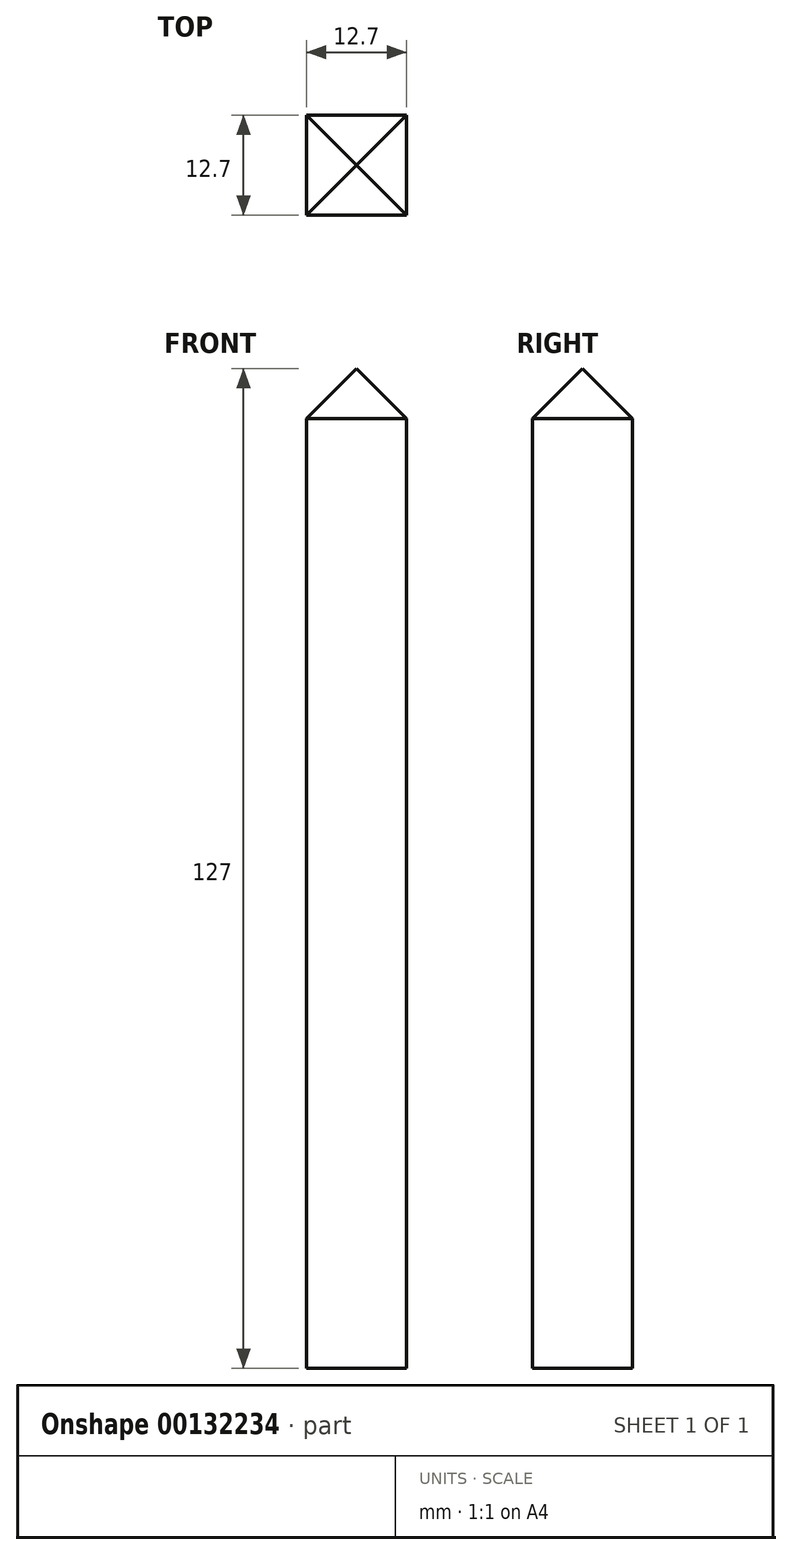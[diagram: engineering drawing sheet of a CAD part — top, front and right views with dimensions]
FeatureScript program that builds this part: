
annotation { "Feature Type Name" : "Feature", "Feature Type Description" : "" }
export const myFeature = defineFeature(function(context is Context, id is Id, definition is map)
    precondition{}
    {
        {
            var Q0;
            Q0=qCreatedBy(makeId("Top.planeOp"),FACE);
            var sketch = newSketch(context, id + "F0", { "sketchPlane" : qUnion([Q0])});
            skLineSegment(sketch, "E0", {"start": v(-37.01, 1.07) * mm, "end": v(-24.31, 1.07) * mm});
            skLineSegment(sketch, "E1", {"start": v(-24.31, 1.07) * mm, "end": v(-24.31, -11.63) * mm});
            skLineSegment(sketch, "E2", {"start": v(-24.31, -11.63) * mm, "end": v(-37.01, -11.63) * mm});
            skLineSegment(sketch, "E3", {"start": v(-37.01, -11.63) * mm, "end": v(-37.01, 1.07) * mm});
            skSolve(sketch);
        }
        {
            var Q0;
            Q0=makeQuery(id+"F0.imprint","IMPRINT",FACE,{"disambiguationData":[TD([[makeQuery(id+"F0.imprint","IMPRINT",EDGE,{"derivedFrom":sQuery(id+"F0.wireOp",EDGE,"E0")}),-1.0]])]});
            extrude(context, id + "F1", {"entities" : qUnion([Q0]), "depth" : 127 * mm});
        }
        {
            var Q0;
            Q0=makeQuery(id+"F1.opExtrude","CAP_EDGE",EDGE,{"disambiguationData":[OSD([sQuery(id+"F0.wireOp",EDGE,"E3")])],"isStart":false});
            var Q1;
            Q1=makeQuery(id+"F1.opExtrude","CAP_EDGE",EDGE,{"disambiguationData":[OSD([sQuery(id+"F0.wireOp",EDGE,"E1")])],"isStart":false});
            var Q2;
            Q2=makeQuery(id+"F1.opExtrude","CAP_EDGE",EDGE,{"disambiguationData":[OSD([sQuery(id+"F0.wireOp",EDGE,"E2")])],"isStart":false});
            var Q3;
            Q3=makeQuery(id+"F1.opExtrude","CAP_EDGE",EDGE,{"disambiguationData":[OSD([sQuery(id+"F0.wireOp",EDGE,"E0")])],"isStart":false});
            chamfer(context, id + "F2", {"entities" : qUnion([Q0, Q1, Q2, Q3]), "width" : 6.35 * mm, "tangentPropagation" : true});
        }
    });
